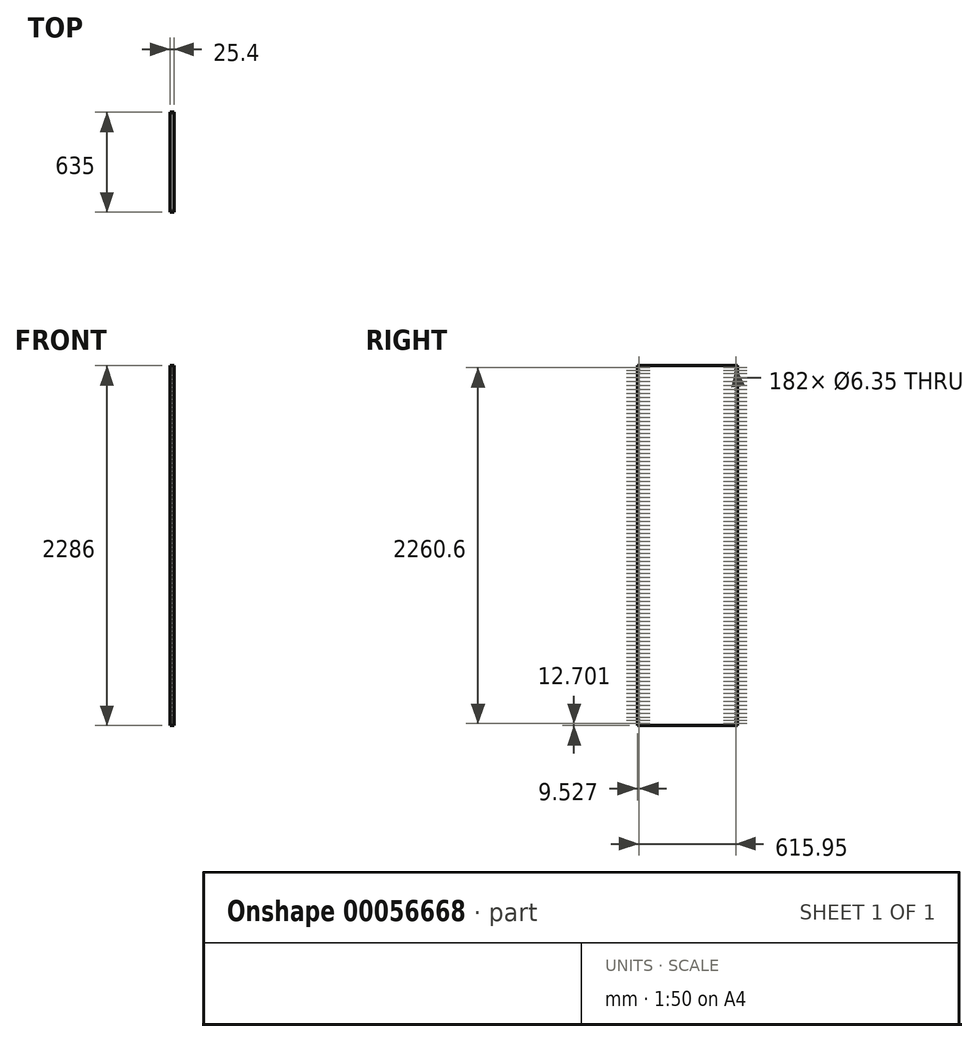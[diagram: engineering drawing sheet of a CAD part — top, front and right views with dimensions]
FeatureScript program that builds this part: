
annotation { "Feature Type Name" : "Feature", "Feature Type Description" : "" }
export const myFeature = defineFeature(function(context is Context, id is Id, definition is map)
    precondition{}
    {
        {
            var Q0;
            Q0=qCreatedBy(makeId("Right.planeOp"),FACE);
            var sketch = newSketch(context, id + "F0", { "sketchPlane" : qUnion([Q0])});
            skLineSegment(sketch, "E0.bottom", {"start": v(-349.17, 644.74) * mm, "end": v(285.83, 644.74) * mm});
            skLineSegment(sketch, "E0.top", {"start": v(-349.17, -1641.26) * mm, "end": v(285.83, -1641.26) * mm});
            skLineSegment(sketch, "E0.left", {"start": v(-349.17, 644.74) * mm, "end": v(-349.17, -1641.26) * mm});
            skLineSegment(sketch, "E0.right", {"start": v(285.83, 644.74) * mm, "end": v(285.83, -1641.26) * mm});
            skCircle(sketch, "E1", {"center": v(-339.64, 593.94) * mm, "radius": 3.17 * mm});
            skCircle(sketch, "E2.0.1.0", {"center": v(-339.64, 568.54) * mm, "radius": 3.17 * mm});
            skCircle(sketch, "E2.0.2.0", {"center": v(-339.64, 543.14) * mm, "radius": 3.17 * mm});
            skCircle(sketch, "E2.0.3.0", {"center": v(-339.64, 517.74) * mm, "radius": 3.17 * mm});
            skCircle(sketch, "E2.0.4.0", {"center": v(-339.64, 492.34) * mm, "radius": 3.17 * mm});
            skCircle(sketch, "E2.0.5.0", {"center": v(-339.64, 466.94) * mm, "radius": 3.17 * mm});
            skCircle(sketch, "E2.0.6.0", {"center": v(-339.64, 441.54) * mm, "radius": 3.17 * mm});
            skCircle(sketch, "E2.0.7.0", {"center": v(-339.64, 416.14) * mm, "radius": 3.17 * mm});
            skCircle(sketch, "E2.0.8.0", {"center": v(-339.64, 390.74) * mm, "radius": 3.17 * mm});
            skCircle(sketch, "E2.0.9.0", {"center": v(-339.64, 365.34) * mm, "radius": 3.17 * mm});
            skCircle(sketch, "E2.0.10.0", {"center": v(-339.64, 339.94) * mm, "radius": 3.17 * mm});
            skCircle(sketch, "E2.0.11.0", {"center": v(-339.64, 314.54) * mm, "radius": 3.17 * mm});
            skCircle(sketch, "E2.0.12.0", {"center": v(-339.64, 289.14) * mm, "radius": 3.17 * mm});
            skCircle(sketch, "E2.0.13.0", {"center": v(-339.64, 263.74) * mm, "radius": 3.17 * mm});
            skCircle(sketch, "E2.0.14.0", {"center": v(-339.64, 238.34) * mm, "radius": 3.17 * mm});
            skCircle(sketch, "E2.0.15.0", {"center": v(-339.64, 212.94) * mm, "radius": 3.17 * mm});
            skCircle(sketch, "E2.0.16.0", {"center": v(-339.64, 187.54) * mm, "radius": 3.17 * mm});
            skCircle(sketch, "E2.0.17.0", {"center": v(-339.64, 162.14) * mm, "radius": 3.17 * mm});
            skCircle(sketch, "E2.0.18.0", {"center": v(-339.64, 136.74) * mm, "radius": 3.17 * mm});
            skCircle(sketch, "E2.0.19.0", {"center": v(-339.64, 111.34) * mm, "radius": 3.17 * mm});
            skCircle(sketch, "E2.0.20.0", {"center": v(-339.64, 85.94) * mm, "radius": 3.17 * mm});
            skCircle(sketch, "E2.0.21.0", {"center": v(-339.64, 60.54) * mm, "radius": 3.17 * mm});
            skCircle(sketch, "E2.0.22.0", {"center": v(-339.64, 35.14) * mm, "radius": 3.17 * mm});
            skCircle(sketch, "E2.0.23.0", {"center": v(-339.64, 9.74) * mm, "radius": 3.17 * mm});
            skCircle(sketch, "E2.0.24.0", {"center": v(-339.64, -15.66) * mm, "radius": 3.17 * mm});
            skCircle(sketch, "E2.0.25.0", {"center": v(-339.64, -41.06) * mm, "radius": 3.17 * mm});
            skCircle(sketch, "E2.0.26.0", {"center": v(-339.64, -66.46) * mm, "radius": 3.17 * mm});
            skCircle(sketch, "E2.0.27.0", {"center": v(-339.64, -91.86) * mm, "radius": 3.17 * mm});
            skCircle(sketch, "E2.0.28.0", {"center": v(-339.64, -117.26) * mm, "radius": 3.17 * mm});
            skCircle(sketch, "E2.0.29.0", {"center": v(-339.64, -142.66) * mm, "radius": 3.17 * mm});
            skCircle(sketch, "E2.0.30.0", {"center": v(-339.64, -168.06) * mm, "radius": 3.17 * mm});
            skCircle(sketch, "E2.0.31.0", {"center": v(-339.64, -193.46) * mm, "radius": 3.17 * mm});
            skCircle(sketch, "E2.0.32.0", {"center": v(-339.64, -218.86) * mm, "radius": 3.17 * mm});
            skCircle(sketch, "E2.0.33.0", {"center": v(-339.64, -244.26) * mm, "radius": 3.17 * mm});
            skCircle(sketch, "E2.0.34.0", {"center": v(-339.64, -269.66) * mm, "radius": 3.17 * mm});
            skCircle(sketch, "E2.0.35.0", {"center": v(-339.64, -295.06) * mm, "radius": 3.17 * mm});
            skCircle(sketch, "E2.0.36.0", {"center": v(-339.64, -320.46) * mm, "radius": 3.17 * mm});
            skCircle(sketch, "E2.0.37.0", {"center": v(-339.64, -345.86) * mm, "radius": 3.17 * mm});
            skCircle(sketch, "E2.0.38.0", {"center": v(-339.64, -371.26) * mm, "radius": 3.17 * mm});
            skCircle(sketch, "E2.0.39.0", {"center": v(-339.64, -396.66) * mm, "radius": 3.17 * mm});
            skCircle(sketch, "E2.0.40.0", {"center": v(-339.64, -422.06) * mm, "radius": 3.17 * mm});
            skCircle(sketch, "E2.0.41.0", {"center": v(-339.64, -447.46) * mm, "radius": 3.17 * mm});
            skCircle(sketch, "E2.0.42.0", {"center": v(-339.64, -472.86) * mm, "radius": 3.17 * mm});
            skCircle(sketch, "E2.0.43.0", {"center": v(-339.64, -498.26) * mm, "radius": 3.17 * mm});
            skCircle(sketch, "E2.0.44.0", {"center": v(-339.64, -523.66) * mm, "radius": 3.17 * mm});
            skCircle(sketch, "E2.0.45.0", {"center": v(-339.64, -549.06) * mm, "radius": 3.17 * mm});
            skCircle(sketch, "E2.0.46.0", {"center": v(-339.64, -574.46) * mm, "radius": 3.17 * mm});
            skCircle(sketch, "E2.0.47.0", {"center": v(-339.64, -599.86) * mm, "radius": 3.17 * mm});
            skCircle(sketch, "E2.0.48.0", {"center": v(-339.64, -625.26) * mm, "radius": 3.17 * mm});
            skCircle(sketch, "E2.0.49.0", {"center": v(-339.64, -650.66) * mm, "radius": 3.17 * mm});
            skCircle(sketch, "E2.0.50.0", {"center": v(-339.64, -676.06) * mm, "radius": 3.17 * mm});
            skCircle(sketch, "E2.0.51.0", {"center": v(-339.64, -701.46) * mm, "radius": 3.17 * mm});
            skCircle(sketch, "E2.0.52.0", {"center": v(-339.64, -726.86) * mm, "radius": 3.17 * mm});
            skCircle(sketch, "E2.0.53.0", {"center": v(-339.64, -752.26) * mm, "radius": 3.17 * mm});
            skCircle(sketch, "E2.0.54.0", {"center": v(-339.64, -777.66) * mm, "radius": 3.17 * mm});
            skCircle(sketch, "E2.0.55.0", {"center": v(-339.64, -803.06) * mm, "radius": 3.17 * mm});
            skCircle(sketch, "E2.0.56.0", {"center": v(-339.64, -828.46) * mm, "radius": 3.17 * mm});
            skCircle(sketch, "E2.0.57.0", {"center": v(-339.64, -853.86) * mm, "radius": 3.17 * mm});
            skCircle(sketch, "E2.0.58.0", {"center": v(-339.64, -879.26) * mm, "radius": 3.17 * mm});
            skCircle(sketch, "E2.0.59.0", {"center": v(-339.64, -904.66) * mm, "radius": 3.17 * mm});
            skCircle(sketch, "E2.0.60.0", {"center": v(-339.64, -930.06) * mm, "radius": 3.17 * mm});
            skCircle(sketch, "E2.0.61.0", {"center": v(-339.64, -955.46) * mm, "radius": 3.17 * mm});
            skCircle(sketch, "E2.0.62.0", {"center": v(-339.64, -980.86) * mm, "radius": 3.17 * mm});
            skCircle(sketch, "E2.0.63.0", {"center": v(-339.64, -1006.26) * mm, "radius": 3.17 * mm});
            skCircle(sketch, "E2.0.64.0", {"center": v(-339.64, -1031.66) * mm, "radius": 3.17 * mm});
            skCircle(sketch, "E2.0.65.0", {"center": v(-339.64, -1057.06) * mm, "radius": 3.17 * mm});
            skCircle(sketch, "E2.0.66.0", {"center": v(-339.64, -1082.46) * mm, "radius": 3.17 * mm});
            skCircle(sketch, "E2.0.67.0", {"center": v(-339.64, -1107.86) * mm, "radius": 3.17 * mm});
            skCircle(sketch, "E2.0.68.0", {"center": v(-339.64, -1133.26) * mm, "radius": 3.17 * mm});
            skCircle(sketch, "E2.0.69.0", {"center": v(-339.64, -1158.66) * mm, "radius": 3.17 * mm});
            skCircle(sketch, "E2.0.70.0", {"center": v(-339.64, -1184.06) * mm, "radius": 3.17 * mm});
            skCircle(sketch, "E2.0.71.0", {"center": v(-339.64, -1209.46) * mm, "radius": 3.17 * mm});
            skCircle(sketch, "E2.0.72.0", {"center": v(-339.64, -1234.86) * mm, "radius": 3.17 * mm});
            skCircle(sketch, "E2.0.73.0", {"center": v(-339.64, -1260.26) * mm, "radius": 3.17 * mm});
            skCircle(sketch, "E2.0.74.0", {"center": v(-339.64, -1285.66) * mm, "radius": 3.17 * mm});
            skCircle(sketch, "E2.0.75.0", {"center": v(-339.64, -1311.06) * mm, "radius": 3.17 * mm});
            skCircle(sketch, "E2.0.76.0", {"center": v(-339.64, -1336.46) * mm, "radius": 3.17 * mm});
            skCircle(sketch, "E2.0.77.0", {"center": v(-339.64, -1361.86) * mm, "radius": 3.17 * mm});
            skCircle(sketch, "E2.0.78.0", {"center": v(-339.64, -1387.26) * mm, "radius": 3.17 * mm});
            skCircle(sketch, "E2.0.79.0", {"center": v(-339.64, -1412.66) * mm, "radius": 3.17 * mm});
            skCircle(sketch, "E2.0.80.0", {"center": v(-339.64, -1438.06) * mm, "radius": 3.17 * mm});
            skCircle(sketch, "E2.0.81.0", {"center": v(-339.64, -1463.46) * mm, "radius": 3.17 * mm});
            skCircle(sketch, "E2.0.82.0", {"center": v(-339.64, -1488.86) * mm, "radius": 3.17 * mm});
            skCircle(sketch, "E2.0.83.0", {"center": v(-339.64, -1514.26) * mm, "radius": 3.17 * mm});
            skCircle(sketch, "E2.0.84.0", {"center": v(-339.64, -1539.66) * mm, "radius": 3.17 * mm});
            skCircle(sketch, "E2.0.85.0", {"center": v(-339.64, -1565.06) * mm, "radius": 3.17 * mm});
            skCircle(sketch, "E2.0.86.0", {"center": v(-339.64, -1590.46) * mm, "radius": 3.17 * mm});
            skCircle(sketch, "E2.1.0.0", {"center": v(276.3, 593.94) * mm, "radius": 3.17 * mm});
            skCircle(sketch, "E2.1.1.0", {"center": v(276.3, 568.54) * mm, "radius": 3.17 * mm});
            skCircle(sketch, "E2.1.2.0", {"center": v(276.3, 543.14) * mm, "radius": 3.17 * mm});
            skCircle(sketch, "E2.1.3.0", {"center": v(276.3, 517.74) * mm, "radius": 3.17 * mm});
            skCircle(sketch, "E2.1.4.0", {"center": v(276.3, 492.34) * mm, "radius": 3.17 * mm});
            skCircle(sketch, "E2.1.5.0", {"center": v(276.3, 466.94) * mm, "radius": 3.17 * mm});
            skCircle(sketch, "E2.1.6.0", {"center": v(276.3, 441.54) * mm, "radius": 3.17 * mm});
            skCircle(sketch, "E2.1.7.0", {"center": v(276.3, 416.14) * mm, "radius": 3.17 * mm});
            skCircle(sketch, "E2.1.8.0", {"center": v(276.3, 390.74) * mm, "radius": 3.17 * mm});
            skCircle(sketch, "E2.1.9.0", {"center": v(276.3, 365.34) * mm, "radius": 3.17 * mm});
            skCircle(sketch, "E2.1.10.0", {"center": v(276.3, 339.94) * mm, "radius": 3.17 * mm});
            skCircle(sketch, "E2.1.11.0", {"center": v(276.3, 314.54) * mm, "radius": 3.17 * mm});
            skCircle(sketch, "E2.1.12.0", {"center": v(276.3, 289.14) * mm, "radius": 3.17 * mm});
            skCircle(sketch, "E2.1.13.0", {"center": v(276.3, 263.74) * mm, "radius": 3.17 * mm});
            skCircle(sketch, "E2.1.14.0", {"center": v(276.3, 238.34) * mm, "radius": 3.17 * mm});
            skCircle(sketch, "E2.1.15.0", {"center": v(276.3, 212.94) * mm, "radius": 3.17 * mm});
            skCircle(sketch, "E2.1.16.0", {"center": v(276.3, 187.54) * mm, "radius": 3.17 * mm});
            skCircle(sketch, "E2.1.17.0", {"center": v(276.3, 162.14) * mm, "radius": 3.17 * mm});
            skCircle(sketch, "E2.1.18.0", {"center": v(276.3, 136.74) * mm, "radius": 3.17 * mm});
            skCircle(sketch, "E2.1.19.0", {"center": v(276.3, 111.34) * mm, "radius": 3.17 * mm});
            skCircle(sketch, "E2.1.20.0", {"center": v(276.3, 85.94) * mm, "radius": 3.17 * mm});
            skCircle(sketch, "E2.1.21.0", {"center": v(276.3, 60.54) * mm, "radius": 3.17 * mm});
            skCircle(sketch, "E2.1.22.0", {"center": v(276.3, 35.14) * mm, "radius": 3.17 * mm});
            skCircle(sketch, "E2.1.23.0", {"center": v(276.3, 9.74) * mm, "radius": 3.17 * mm});
            skCircle(sketch, "E2.1.24.0", {"center": v(276.3, -15.66) * mm, "radius": 3.17 * mm});
            skCircle(sketch, "E2.1.25.0", {"center": v(276.3, -41.06) * mm, "radius": 3.17 * mm});
            skCircle(sketch, "E2.1.26.0", {"center": v(276.3, -66.46) * mm, "radius": 3.17 * mm});
            skCircle(sketch, "E2.1.27.0", {"center": v(276.3, -91.86) * mm, "radius": 3.17 * mm});
            skCircle(sketch, "E2.1.28.0", {"center": v(276.3, -117.26) * mm, "radius": 3.17 * mm});
            skCircle(sketch, "E2.1.29.0", {"center": v(276.3, -142.66) * mm, "radius": 3.17 * mm});
            skCircle(sketch, "E2.1.30.0", {"center": v(276.3, -168.06) * mm, "radius": 3.17 * mm});
            skCircle(sketch, "E2.1.31.0", {"center": v(276.3, -193.46) * mm, "radius": 3.17 * mm});
            skCircle(sketch, "E2.1.32.0", {"center": v(276.3, -218.86) * mm, "radius": 3.17 * mm});
            skCircle(sketch, "E2.1.33.0", {"center": v(276.3, -244.26) * mm, "radius": 3.17 * mm});
            skCircle(sketch, "E2.1.34.0", {"center": v(276.3, -269.66) * mm, "radius": 3.17 * mm});
            skCircle(sketch, "E2.1.35.0", {"center": v(276.3, -295.06) * mm, "radius": 3.17 * mm});
            skCircle(sketch, "E2.1.36.0", {"center": v(276.3, -320.46) * mm, "radius": 3.17 * mm});
            skCircle(sketch, "E2.1.37.0", {"center": v(276.3, -345.86) * mm, "radius": 3.17 * mm});
            skCircle(sketch, "E2.1.38.0", {"center": v(276.3, -371.26) * mm, "radius": 3.17 * mm});
            skCircle(sketch, "E2.1.39.0", {"center": v(276.3, -396.66) * mm, "radius": 3.17 * mm});
            skCircle(sketch, "E2.1.40.0", {"center": v(276.3, -422.06) * mm, "radius": 3.17 * mm});
            skCircle(sketch, "E2.1.41.0", {"center": v(276.3, -447.46) * mm, "radius": 3.17 * mm});
            skCircle(sketch, "E2.1.42.0", {"center": v(276.3, -472.86) * mm, "radius": 3.17 * mm});
            skCircle(sketch, "E2.1.43.0", {"center": v(276.3, -498.26) * mm, "radius": 3.17 * mm});
            skCircle(sketch, "E2.1.44.0", {"center": v(276.3, -523.66) * mm, "radius": 3.17 * mm});
            skCircle(sketch, "E2.1.45.0", {"center": v(276.3, -549.06) * mm, "radius": 3.17 * mm});
            skCircle(sketch, "E2.1.46.0", {"center": v(276.3, -574.46) * mm, "radius": 3.17 * mm});
            skCircle(sketch, "E2.1.47.0", {"center": v(276.3, -599.86) * mm, "radius": 3.17 * mm});
            skCircle(sketch, "E2.1.48.0", {"center": v(276.3, -625.26) * mm, "radius": 3.17 * mm});
            skCircle(sketch, "E2.1.49.0", {"center": v(276.3, -650.66) * mm, "radius": 3.17 * mm});
            skCircle(sketch, "E2.1.50.0", {"center": v(276.3, -676.06) * mm, "radius": 3.17 * mm});
            skCircle(sketch, "E2.1.51.0", {"center": v(276.3, -701.46) * mm, "radius": 3.17 * mm});
            skCircle(sketch, "E2.1.52.0", {"center": v(276.3, -726.86) * mm, "radius": 3.17 * mm});
            skCircle(sketch, "E2.1.53.0", {"center": v(276.3, -752.26) * mm, "radius": 3.17 * mm});
            skCircle(sketch, "E2.1.54.0", {"center": v(276.3, -777.66) * mm, "radius": 3.17 * mm});
            skCircle(sketch, "E2.1.55.0", {"center": v(276.3, -803.06) * mm, "radius": 3.17 * mm});
            skCircle(sketch, "E2.1.56.0", {"center": v(276.3, -828.46) * mm, "radius": 3.17 * mm});
            skCircle(sketch, "E2.1.57.0", {"center": v(276.3, -853.86) * mm, "radius": 3.17 * mm});
            skCircle(sketch, "E2.1.58.0", {"center": v(276.3, -879.26) * mm, "radius": 3.17 * mm});
            skCircle(sketch, "E2.1.59.0", {"center": v(276.3, -904.66) * mm, "radius": 3.17 * mm});
            skCircle(sketch, "E2.1.60.0", {"center": v(276.3, -930.06) * mm, "radius": 3.17 * mm});
            skCircle(sketch, "E2.1.61.0", {"center": v(276.3, -955.46) * mm, "radius": 3.17 * mm});
            skCircle(sketch, "E2.1.62.0", {"center": v(276.3, -980.86) * mm, "radius": 3.17 * mm});
            skCircle(sketch, "E2.1.63.0", {"center": v(276.3, -1006.26) * mm, "radius": 3.17 * mm});
            skCircle(sketch, "E2.1.64.0", {"center": v(276.3, -1031.66) * mm, "radius": 3.17 * mm});
            skCircle(sketch, "E2.1.65.0", {"center": v(276.3, -1057.06) * mm, "radius": 3.17 * mm});
            skCircle(sketch, "E2.1.66.0", {"center": v(276.3, -1082.46) * mm, "radius": 3.17 * mm});
            skCircle(sketch, "E2.1.67.0", {"center": v(276.3, -1107.86) * mm, "radius": 3.17 * mm});
            skCircle(sketch, "E2.1.68.0", {"center": v(276.3, -1133.26) * mm, "radius": 3.17 * mm});
            skCircle(sketch, "E2.1.69.0", {"center": v(276.3, -1158.66) * mm, "radius": 3.17 * mm});
            skCircle(sketch, "E2.1.70.0", {"center": v(276.3, -1184.06) * mm, "radius": 3.17 * mm});
            skCircle(sketch, "E2.1.71.0", {"center": v(276.3, -1209.46) * mm, "radius": 3.17 * mm});
            skCircle(sketch, "E2.1.72.0", {"center": v(276.3, -1234.86) * mm, "radius": 3.17 * mm});
            skCircle(sketch, "E2.1.73.0", {"center": v(276.3, -1260.26) * mm, "radius": 3.17 * mm});
            skCircle(sketch, "E2.1.74.0", {"center": v(276.3, -1285.66) * mm, "radius": 3.17 * mm});
            skCircle(sketch, "E2.1.75.0", {"center": v(276.3, -1311.06) * mm, "radius": 3.17 * mm});
            skCircle(sketch, "E2.1.76.0", {"center": v(276.3, -1336.46) * mm, "radius": 3.17 * mm});
            skCircle(sketch, "E2.1.77.0", {"center": v(276.3, -1361.86) * mm, "radius": 3.17 * mm});
            skCircle(sketch, "E2.1.78.0", {"center": v(276.3, -1387.26) * mm, "radius": 3.17 * mm});
            skCircle(sketch, "E2.1.79.0", {"center": v(276.3, -1412.66) * mm, "radius": 3.17 * mm});
            skCircle(sketch, "E2.1.80.0", {"center": v(276.3, -1438.06) * mm, "radius": 3.17 * mm});
            skCircle(sketch, "E2.1.81.0", {"center": v(276.3, -1463.46) * mm, "radius": 3.17 * mm});
            skCircle(sketch, "E2.1.82.0", {"center": v(276.3, -1488.86) * mm, "radius": 3.17 * mm});
            skCircle(sketch, "E2.1.83.0", {"center": v(276.3, -1514.26) * mm, "radius": 3.17 * mm});
            skCircle(sketch, "E2.1.84.0", {"center": v(276.3, -1539.66) * mm, "radius": 3.17 * mm});
            skCircle(sketch, "E2.1.85.0", {"center": v(276.3, -1565.06) * mm, "radius": 3.17 * mm});
            skCircle(sketch, "E2.1.86.0", {"center": v(276.3, -1590.46) * mm, "radius": 3.17 * mm});
            skLineSegment(sketch, "E2.direction1", {"start": v(-339.64, 593.94) * mm, "end": v(276.3, 593.94) * mm, "construction": true});
            skLineSegment(sketch, "E2.direction2", {"start": v(-339.64, 593.94) * mm, "end": v(-339.64, 568.54) * mm, "construction": true});
            skCircle(sketch, "E3", {"center": v(-339.64, -1628.56) * mm, "radius": 3.18 * mm});
            skCircle(sketch, "E4", {"center": v(-339.64, -1609.5) * mm, "radius": 3.18 * mm});
            skCircle(sketch, "E5.0.1.0", {"center": v(-339.64, 613) * mm, "radius": 3.18 * mm});
            skCircle(sketch, "E5.0.1.1", {"center": v(-339.64, 632.04) * mm, "radius": 3.18 * mm});
            skCircle(sketch, "E5.1.0.0", {"center": v(276.3, -1628.56) * mm, "radius": 3.18 * mm});
            skCircle(sketch, "E5.1.0.1", {"center": v(276.3, -1609.5) * mm, "radius": 3.18 * mm});
            skCircle(sketch, "E5.1.1.0", {"center": v(276.3, 613) * mm, "radius": 3.18 * mm});
            skCircle(sketch, "E5.1.1.1", {"center": v(276.3, 632.04) * mm, "radius": 3.18 * mm});
            skLineSegment(sketch, "E5.direction1", {"start": v(-339.64, -1628.56) * mm, "end": v(276.3, -1628.56) * mm, "construction": true});
            skLineSegment(sketch, "E5.direction2", {"start": v(-339.64, -1628.56) * mm, "end": v(-339.64, 613) * mm, "construction": true});
            skSolve(sketch);
        }
        {
            var Q0;
            Q0 = qSketchRegion(id + "F0", true);
            extrude(context, id + "F1", {"entities" : qUnion([Q0]), "depth" : 25.4 * mm});
        }
    });
